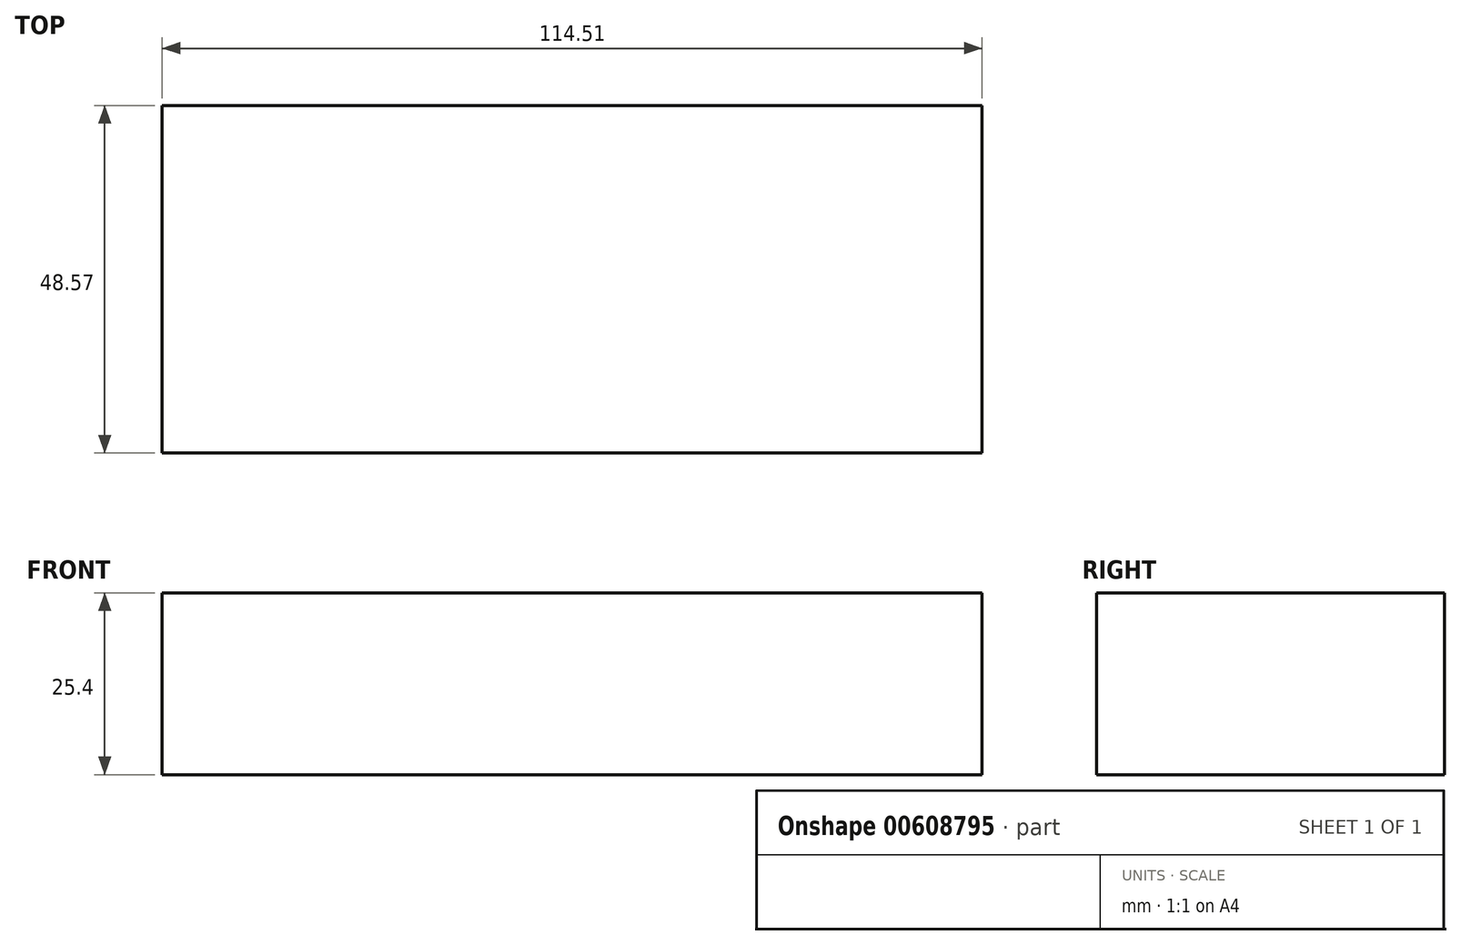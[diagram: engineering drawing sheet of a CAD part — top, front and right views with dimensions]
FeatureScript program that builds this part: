
annotation { "Feature Type Name" : "Feature", "Feature Type Description" : "" }
export const myFeature = defineFeature(function(context is Context, id is Id, definition is map)
    precondition{}
    {
        {
            var Q0;
            Q0=qCreatedBy(makeId("Top.planeOp"),FACE);
            var sketch = newSketch(context, id + "F0", { "sketchPlane" : qUnion([Q0])});
            skLineSegment(sketch, "E0.bottom", {"start": v(-55.86, 26.72) * mm, "end": v(58.65, 26.72) * mm});
            skLineSegment(sketch, "E0.top", {"start": v(-55.86, -21.85) * mm, "end": v(58.65, -21.85) * mm});
            skLineSegment(sketch, "E0.left", {"start": v(-55.86, 26.72) * mm, "end": v(-55.86, -21.85) * mm});
            skLineSegment(sketch, "E0.right", {"start": v(58.65, 26.72) * mm, "end": v(58.65, -21.85) * mm});
            skSolve(sketch);
        }
        {
            var Q0;
            Q0 = qSketchRegion(id + "F0", true);
            extrude(context, id + "F1", {"entities" : qUnion([Q0]), "depth" : 25.4 * mm, "offsetDistance" : 25.4 * mm});
        }
    });
